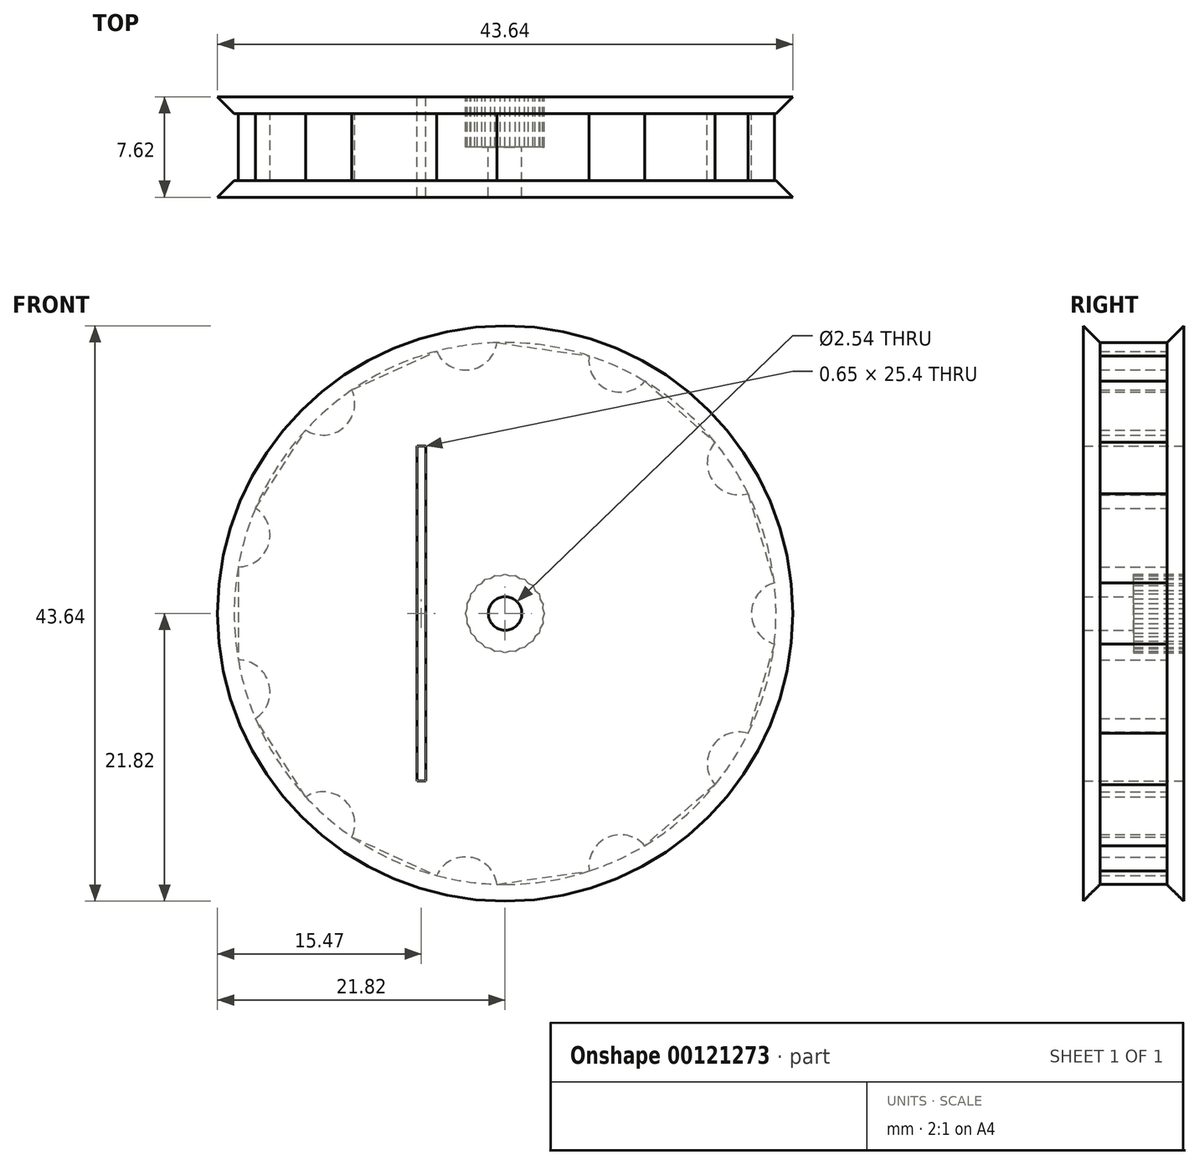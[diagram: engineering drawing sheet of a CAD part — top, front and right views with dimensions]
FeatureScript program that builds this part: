
annotation { "Feature Type Name" : "Feature", "Feature Type Description" : "" }
export const myFeature = defineFeature(function(context is Context, id is Id, definition is map)
    precondition{}
    {
        {
            var Q0;
            Q0=qCreatedBy(makeId("Front.planeOp"),FACE);
            var sketch = newSketch(context, id + "F0", { "sketchPlane" : qUnion([Q0])});
            skCircle(sketch, "E0", {"center": v(21.1, 0) * mm, "radius": 2.41 * mm});
            skCircle(sketch, "E1.1.0", {"center": v(17.75, 11.4) * mm, "radius": 2.41 * mm});
            skCircle(sketch, "E1.2.0", {"center": v(8.76, 19.2) * mm, "radius": 2.41 * mm});
            skCircle(sketch, "E1.3.0", {"center": v(-3, 20.88) * mm, "radius": 2.41 * mm});
            skCircle(sketch, "E1.4.0", {"center": v(-13.82, 15.94) * mm, "radius": 2.41 * mm});
            skCircle(sketch, "E1.5.0", {"center": v(-20.24, 5.94) * mm, "radius": 2.41 * mm});
            skPoint(sketch, "E1.center", {"position": v(0, 0) * mm});
            skCircle(sketch, "E2.1.6.0", {"center": v(-20.24, -5.94) * mm, "radius": 2.41 * mm});
            skLineSegment(sketch, "E3", {"start": v(-3, 20.88) * mm, "end": v(8.76, 19.2) * mm});
            skLineSegment(sketch, "E4", {"start": v(8.76, 19.2) * mm, "end": v(17.75, 11.4) * mm});
            skLineSegment(sketch, "E5", {"start": v(17.75, 11.4) * mm, "end": v(21.1, 0) * mm});
            skLineSegment(sketch, "E6", {"start": v(21.1, 0) * mm, "end": v(17.75, -11.4) * mm});
            skLineSegment(sketch, "E7", {"start": v(-20.24, 5.94) * mm, "end": v(-13.82, 15.94) * mm});
            skLineSegment(sketch, "E8", {"start": v(-13.82, 15.94) * mm, "end": v(-3, 20.88) * mm});
            skCircle(sketch, "E9.1.7.0", {"center": v(-13.82, -15.94) * mm, "radius": 2.41 * mm});
            skCircle(sketch, "E9.1.8.0", {"center": v(-3, -20.88) * mm, "radius": 2.41 * mm});
            skCircle(sketch, "E9.1.9.0", {"center": v(8.76, -19.2) * mm, "radius": 2.41 * mm});
            skLineSegment(sketch, "E10", {"start": v(-20.24, 5.94) * mm, "end": v(-20.24, -5.94) * mm});
            skLineSegment(sketch, "E11", {"start": v(-13.82, -15.94) * mm, "end": v(-20.24, -5.94) * mm});
            skLineSegment(sketch, "E12", {"start": v(-13.82, -15.94) * mm, "end": v(-3, -20.88) * mm});
            skCircle(sketch, "E13.1.10.0", {"center": v(17.75, -11.4) * mm, "radius": 2.41 * mm});
            skLineSegment(sketch, "E14", {"start": v(-3, -20.88) * mm, "end": v(8.76, -19.2) * mm});
            skLineSegment(sketch, "E15", {"start": v(17.75, -11.4) * mm, "end": v(8.76, -19.2) * mm});
            skCircle(sketch, "E16", {"center": v(0, 0) * mm, "radius": 1.27 * mm});
            skLineSegment(sketch, "E17", {"start": v(0, 0) * mm, "end": v(-6.35, 0) * mm, "construction": true});
            skLineSegment(sketch, "E18.bottom", {"start": v(-6.03, 12.7) * mm, "end": v(-6.67, 12.7) * mm});
            skLineSegment(sketch, "E18.top", {"start": v(-6.03, -12.7) * mm, "end": v(-6.67, -12.7) * mm});
            skLineSegment(sketch, "E18.left", {"start": v(-6.03, 12.7) * mm, "end": v(-6.03, -12.7) * mm});
            skLineSegment(sketch, "E18.right", {"start": v(-6.67, 12.7) * mm, "end": v(-6.67, -12.7) * mm});
            skPoint(sketch, "E18.middle", {"position": v(-6.35, 0) * mm});
            skSolve(sketch);
        }
        {
            var Q0;
            {var subQ22=sQuery(id+"F0.wireOp",EDGE,"E5");var subQ23=sQuery(id+"F0.wireOp",EDGE,"E0");var subQ24=makeQuery(id+"F0.imprint","INTERSECT",VERTEX,{"derivedFrom":[subQ23,subQ22]});Q0=makeQuery(id+"F0.imprint","IMPRINT",FACE,{"disambiguationData":[TD([[makeQuery(id+"F0.imprint","IMPRINT",EDGE,{"disambiguationData":[TD([[subQ24,-1.0]])],"derivedFrom":subQ23}),-1.0]])]});}
            extrude(context, id + "F1", {"entities" : qUnion([Q0]), "endBound" : BoundingType.SYMMETRIC, "depth" : 5.08 * mm});
        }
        {
            var Q0;
            Q0=makeQuery(id+"F1.opExtrude","CAP_FACE",FACE,{"disambiguationData":[OSD([sQuery(id+"F0.wireOp",EDGE,"E0"),sQuery(id+"F0.wireOp",EDGE,"E1.1.0"),sQuery(id+"F0.wireOp",EDGE,"E1.2.0"),sQuery(id+"F0.wireOp",EDGE,"E1.3.0"),sQuery(id+"F0.wireOp",EDGE,"E1.4.0"),sQuery(id+"F0.wireOp",EDGE,"E1.5.0"),sQuery(id+"F0.wireOp",EDGE,"E2.1.6.0"),sQuery(id+"F0.wireOp",EDGE,"E3"),sQuery(id+"F0.wireOp",EDGE,"E4"),sQuery(id+"F0.wireOp",EDGE,"E5"),sQuery(id+"F0.wireOp",EDGE,"E6"),sQuery(id+"F0.wireOp",EDGE,"k3TeTAbi-IA3Q-FxME-Idnx-3CxbzsMN8JZN"),sQuery(id+"F0.wireOp",EDGE,"E7"),sQuery(id+"F0.wireOp",EDGE,"E8")])],"isStart":false});
            var sketch = newSketch(context, id + "F2", { "sketchPlane" : qUnion([Q0])});
            skCircle(sketch, "E19", {"center": v(0, 0) * mm, "radius": 21.82 * mm});
            skCircle(sketch, "E20", {"center": v(0, 0) * mm, "radius": 1.27 * mm});
            skLineSegment(sketch, "E21", {"start": v(0, 0) * mm, "end": v(-6.35, 0) * mm, "construction": true});
            skLineSegment(sketch, "E22.bottom", {"start": v(-6.03, 12.7) * mm, "end": v(-6.67, 12.7) * mm});
            skLineSegment(sketch, "E22.top", {"start": v(-6.03, -12.7) * mm, "end": v(-6.67, -12.7) * mm});
            skLineSegment(sketch, "E22.left", {"start": v(-6.03, 12.7) * mm, "end": v(-6.03, -12.7) * mm});
            skLineSegment(sketch, "E22.right", {"start": v(-6.67, 12.7) * mm, "end": v(-6.67, -12.7) * mm});
            skPoint(sketch, "E22.middle", {"position": v(-6.35, 0) * mm});
            skSolve(sketch);
        }
        {
            var Q0;
            Q0 = qSketchRegion(id + "F2", true);
            extrude(context, id + "F3", {"entities" : qUnion([Q0]), "operationType" : NewBodyOperationType.ADD, "depth" : 1.27 * mm});
        }
        {
            var Q0;
            Q0=makeQuery(id+"F3.opExtrude","CAP_EDGE",EDGE,{"disambiguationData":[OSD([sQuery(id+"F2.wireOp",EDGE,"E19")])],"isStart":true});
            chamfer(context, id + "F4", {"entities" : qUnion([Q0]), "width" : 1.27 * mm, "tangentPropagation" : true});
        }
        {
            var Q0;
            Q0=makeQuery(id+"F1.opExtrude","SWEPT_BODY",BODY,{"disambiguationData":[OSD([sQuery(id+"F0.wireOp",EDGE,"E0"),sQuery(id+"F0.wireOp",EDGE,"E1.1.0"),sQuery(id+"F0.wireOp",EDGE,"E1.2.0"),sQuery(id+"F0.wireOp",EDGE,"E1.3.0"),sQuery(id+"F0.wireOp",EDGE,"E1.4.0"),sQuery(id+"F0.wireOp",EDGE,"E1.5.0"),sQuery(id+"F0.wireOp",EDGE,"E2.1.6.0"),sQuery(id+"F0.wireOp",EDGE,"E3"),sQuery(id+"F0.wireOp",EDGE,"E4"),sQuery(id+"F0.wireOp",EDGE,"E5"),sQuery(id+"F0.wireOp",EDGE,"E6"),sQuery(id+"F0.wireOp",EDGE,"k3TeTAbi-IA3Q-FxME-Idnx-3CxbzsMN8JZN"),sQuery(id+"F0.wireOp",EDGE,"E7"),sQuery(id+"F0.wireOp",EDGE,"E8")])]});
            var Q1;
            Q1=qCreatedBy(makeId("Front.planeOp"),FACE);
            mirror(context, id + "F5", {"operationType" : NewBodyOperationType.ADD, "entities" : qUnion([Q0]), "mirrorPlane" : qUnion([Q1])});
        }
        {
            var Q0;
            Q0=makeQuery(id+"F5.opPattern","COPY",FACE,{"derivedFrom":makeQuery(id+"F3.opExtrude","CAP_FACE",FACE,{"disambiguationData":[OSD([sQuery(id+"F2.wireOp",EDGE,"E19")])],"isStart":false}),"instanceName":"1"});
            var sketch = newSketch(context, id + "F6", { "sketchPlane" : qUnion([Q0])});
            skCircle(sketch, "E23.cCircle", {"center": v(0, 0) * mm, "radius": 2.86 * mm, "construction": true});
            skLineSegment(sketch, "E23.0", {"start": v(2.66, -1.1) * mm, "end": v(2.29, -1.75) * mm, "construction": true});
            skLineSegment(sketch, "E23.1", {"start": v(2.29, -1.75) * mm, "end": v(1.75, -2.29) * mm, "construction": true});
            skLineSegment(sketch, "E23.2", {"start": v(1.75, -2.29) * mm, "end": v(1.1, -2.66) * mm, "construction": true});
            skLineSegment(sketch, "E23.3", {"start": v(1.1, -2.66) * mm, "end": v(0.38, -2.86) * mm, "construction": true});
            skLineSegment(sketch, "E23.4", {"start": v(0.38, -2.86) * mm, "end": v(-0.38, -2.86) * mm, "construction": true});
            skLineSegment(sketch, "E23.5", {"start": v(-0.38, -2.86) * mm, "end": v(-1.1, -2.66) * mm, "construction": true});
            skLineSegment(sketch, "E23.6", {"start": v(-1.1, -2.66) * mm, "end": v(-1.75, -2.29) * mm, "construction": true});
            skLineSegment(sketch, "E23.7", {"start": v(-1.75, -2.29) * mm, "end": v(-2.29, -1.75) * mm, "construction": true});
            skLineSegment(sketch, "E23.8", {"start": v(-2.29, -1.75) * mm, "end": v(-2.66, -1.1) * mm, "construction": true});
            skLineSegment(sketch, "E23.9", {"start": v(-2.66, -1.1) * mm, "end": v(-2.86, -0.38) * mm, "construction": true});
            skLineSegment(sketch, "E23.10", {"start": v(-2.86, -0.38) * mm, "end": v(-2.86, 0.38) * mm, "construction": true});
            skLineSegment(sketch, "E23.11", {"start": v(-2.86, 0.38) * mm, "end": v(-2.66, 1.1) * mm, "construction": true});
            skLineSegment(sketch, "E23.12", {"start": v(-2.66, 1.1) * mm, "end": v(-2.29, 1.75) * mm, "construction": true});
            skLineSegment(sketch, "E23.13", {"start": v(-2.29, 1.75) * mm, "end": v(-1.75, 2.29) * mm, "construction": true});
            skLineSegment(sketch, "E23.14", {"start": v(-1.75, 2.29) * mm, "end": v(-1.1, 2.66) * mm, "construction": true});
            skLineSegment(sketch, "E23.15", {"start": v(-1.1, 2.66) * mm, "end": v(-0.38, 2.86) * mm, "construction": true});
            skLineSegment(sketch, "E23.16", {"start": v(-0.38, 2.86) * mm, "end": v(0.38, 2.86) * mm, "construction": true});
            skLineSegment(sketch, "E23.17", {"start": v(0.38, 2.86) * mm, "end": v(1.1, 2.66) * mm, "construction": true});
            skLineSegment(sketch, "E23.18", {"start": v(1.1, 2.66) * mm, "end": v(1.75, 2.29) * mm, "construction": true});
            skLineSegment(sketch, "E23.19", {"start": v(1.75, 2.29) * mm, "end": v(2.29, 1.75) * mm, "construction": true});
            skLineSegment(sketch, "E23.20", {"start": v(2.29, 1.75) * mm, "end": v(2.66, 1.1) * mm, "construction": true});
            skLineSegment(sketch, "E23.21", {"start": v(2.66, 1.1) * mm, "end": v(2.86, 0.38) * mm, "construction": true});
            skLineSegment(sketch, "E23.22", {"start": v(2.86, 0.38) * mm, "end": v(2.86, -0.38) * mm, "construction": true});
            skLineSegment(sketch, "E23.23", {"start": v(2.86, -0.38) * mm, "end": v(2.66, -1.1) * mm, "construction": true});
            skPoint(sketch, "E23.0.midPoint", {"position": v(2.47, -1.43) * mm});
            skCircle(sketch, "E24.cCircle", {"center": v(0, 0) * mm, "radius": 2.98 * mm, "construction": true});
            skLineSegment(sketch, "E24.0", {"start": v(2.88, 0.77) * mm, "end": v(2.98, 0) * mm});
            skLineSegment(sketch, "E24.1", {"start": v(2.98, 0) * mm, "end": v(2.88, -0.77) * mm});
            skLineSegment(sketch, "E24.2", {"start": v(2.88, -0.77) * mm, "end": v(2.58, -1.5) * mm});
            skLineSegment(sketch, "E24.3", {"start": v(2.58, -1.5) * mm, "end": v(2.11, -2.11) * mm});
            skLineSegment(sketch, "E24.4", {"start": v(2.11, -2.11) * mm, "end": v(1.5, -2.58) * mm});
            skLineSegment(sketch, "E24.5", {"start": v(1.5, -2.58) * mm, "end": v(0.77, -2.88) * mm});
            skLineSegment(sketch, "E24.6", {"start": v(0.77, -2.88) * mm, "end": v(0, -2.98) * mm});
            skLineSegment(sketch, "E24.7", {"start": v(0, -2.98) * mm, "end": v(-0.77, -2.88) * mm});
            skLineSegment(sketch, "E24.8", {"start": v(-0.77, -2.88) * mm, "end": v(-1.5, -2.58) * mm});
            skLineSegment(sketch, "E24.9", {"start": v(-1.5, -2.58) * mm, "end": v(-2.11, -2.11) * mm});
            skLineSegment(sketch, "E24.10", {"start": v(-2.11, -2.11) * mm, "end": v(-2.58, -1.5) * mm});
            skLineSegment(sketch, "E24.11", {"start": v(-2.58, -1.5) * mm, "end": v(-2.88, -0.77) * mm});
            skLineSegment(sketch, "E24.12", {"start": v(-2.88, -0.77) * mm, "end": v(-2.98, 0) * mm});
            skLineSegment(sketch, "E24.13", {"start": v(-2.98, 0) * mm, "end": v(-2.88, 0.77) * mm});
            skLineSegment(sketch, "E24.14", {"start": v(-2.88, 0.77) * mm, "end": v(-2.58, 1.5) * mm});
            skLineSegment(sketch, "E24.15", {"start": v(-2.58, 1.5) * mm, "end": v(-2.11, 2.11) * mm});
            skLineSegment(sketch, "E24.16", {"start": v(-2.11, 2.11) * mm, "end": v(-1.5, 2.58) * mm});
            skLineSegment(sketch, "E24.17", {"start": v(-1.5, 2.58) * mm, "end": v(-0.77, 2.88) * mm});
            skLineSegment(sketch, "E24.18", {"start": v(-0.77, 2.88) * mm, "end": v(0, 2.98) * mm});
            skLineSegment(sketch, "E24.19", {"start": v(0, 2.98) * mm, "end": v(0.77, 2.88) * mm});
            skLineSegment(sketch, "E24.20", {"start": v(0.77, 2.88) * mm, "end": v(1.5, 2.58) * mm});
            skLineSegment(sketch, "E24.21", {"start": v(1.5, 2.58) * mm, "end": v(2.11, 2.11) * mm});
            skLineSegment(sketch, "E24.22", {"start": v(2.11, 2.11) * mm, "end": v(2.58, 1.5) * mm});
            skLineSegment(sketch, "E24.23", {"start": v(2.58, 1.5) * mm, "end": v(2.88, 0.77) * mm});
            skLineSegment(sketch, "E25", {"start": v(-2.88, 0.77) * mm, "end": v(-2.66, 1.1) * mm});
            skLineSegment(sketch, "E26", {"start": v(-2.88, 0.77) * mm, "end": v(-2.86, 0.38) * mm});
            skLineSegment(sketch, "E27", {"start": v(0, 0) * mm, "end": v(-3.6, 0) * mm, "construction": true});
            skLineSegment(sketch, "E28", {"start": v(-2.86, 0.38) * mm, "end": v(-2.98, 0) * mm});
            skLineSegment(sketch, "E29", {"start": v(-2.98, 0) * mm, "end": v(-2.86, -0.38) * mm});
            skLineSegment(sketch, "E30.1.0", {"start": v(-2.86, -0.38) * mm, "end": v(-2.88, -0.77) * mm});
            skLineSegment(sketch, "E30.1.1", {"start": v(-2.88, -0.77) * mm, "end": v(-2.66, -1.1) * mm});
            skLineSegment(sketch, "E30.2.0", {"start": v(-2.66, -1.1) * mm, "end": v(-2.58, -1.5) * mm});
            skLineSegment(sketch, "E30.2.1", {"start": v(-2.58, -1.5) * mm, "end": v(-2.29, -1.75) * mm});
            skLineSegment(sketch, "E30.3.0", {"start": v(-2.29, -1.75) * mm, "end": v(-2.11, -2.11) * mm});
            skLineSegment(sketch, "E30.3.1", {"start": v(-2.11, -2.11) * mm, "end": v(-1.75, -2.29) * mm});
            skLineSegment(sketch, "E30.4.0", {"start": v(-1.75, -2.29) * mm, "end": v(-1.5, -2.58) * mm});
            skLineSegment(sketch, "E30.4.1", {"start": v(-1.5, -2.58) * mm, "end": v(-1.1, -2.66) * mm});
            skLineSegment(sketch, "E30.5.0", {"start": v(-1.1, -2.66) * mm, "end": v(-0.77, -2.88) * mm});
            skLineSegment(sketch, "E30.5.1", {"start": v(-0.77, -2.88) * mm, "end": v(-0.38, -2.86) * mm});
            skLineSegment(sketch, "E30.6.0", {"start": v(-0.38, -2.86) * mm, "end": v(0, -2.98) * mm});
            skLineSegment(sketch, "E30.6.1", {"start": v(0, -2.98) * mm, "end": v(0.38, -2.86) * mm});
            skLineSegment(sketch, "E30.7.0", {"start": v(0.38, -2.86) * mm, "end": v(0.77, -2.88) * mm});
            skLineSegment(sketch, "E30.7.1", {"start": v(0.77, -2.88) * mm, "end": v(1.1, -2.66) * mm});
            skLineSegment(sketch, "E30.8.0", {"start": v(1.1, -2.66) * mm, "end": v(1.5, -2.58) * mm});
            skLineSegment(sketch, "E30.8.1", {"start": v(1.5, -2.58) * mm, "end": v(1.75, -2.29) * mm});
            skLineSegment(sketch, "E30.9.0", {"start": v(1.75, -2.29) * mm, "end": v(2.11, -2.11) * mm});
            skLineSegment(sketch, "E30.9.1", {"start": v(2.11, -2.11) * mm, "end": v(2.29, -1.75) * mm});
            skLineSegment(sketch, "E30.10.0", {"start": v(2.29, -1.75) * mm, "end": v(2.58, -1.5) * mm});
            skLineSegment(sketch, "E30.10.1", {"start": v(2.58, -1.5) * mm, "end": v(2.66, -1.1) * mm});
            skLineSegment(sketch, "E30.11.0", {"start": v(2.66, -1.1) * mm, "end": v(2.88, -0.77) * mm});
            skLineSegment(sketch, "E30.11.1", {"start": v(2.88, -0.77) * mm, "end": v(2.86, -0.38) * mm});
            skLineSegment(sketch, "E30.12.0", {"start": v(2.86, -0.38) * mm, "end": v(2.98, 0) * mm});
            skLineSegment(sketch, "E30.12.1", {"start": v(2.98, 0) * mm, "end": v(2.86, 0.38) * mm});
            skLineSegment(sketch, "E30.13.0", {"start": v(2.86, 0.38) * mm, "end": v(2.88, 0.77) * mm});
            skLineSegment(sketch, "E30.13.1", {"start": v(2.88, 0.77) * mm, "end": v(2.66, 1.1) * mm});
            skLineSegment(sketch, "E30.14.0", {"start": v(2.66, 1.1) * mm, "end": v(2.58, 1.5) * mm});
            skLineSegment(sketch, "E30.14.1", {"start": v(2.58, 1.5) * mm, "end": v(2.29, 1.75) * mm});
            skLineSegment(sketch, "E30.15.0", {"start": v(2.29, 1.75) * mm, "end": v(2.11, 2.11) * mm});
            skLineSegment(sketch, "E30.15.1", {"start": v(2.11, 2.11) * mm, "end": v(1.75, 2.29) * mm});
            skLineSegment(sketch, "E30.16.0", {"start": v(1.75, 2.29) * mm, "end": v(1.5, 2.58) * mm});
            skLineSegment(sketch, "E30.16.1", {"start": v(1.5, 2.58) * mm, "end": v(1.1, 2.66) * mm});
            skLineSegment(sketch, "E30.17.0", {"start": v(1.1, 2.66) * mm, "end": v(0.77, 2.88) * mm});
            skLineSegment(sketch, "E30.17.1", {"start": v(0.77, 2.88) * mm, "end": v(0.38, 2.86) * mm});
            skLineSegment(sketch, "E30.18.0", {"start": v(0.38, 2.86) * mm, "end": v(0, 2.98) * mm});
            skLineSegment(sketch, "E30.18.1", {"start": v(0, 2.98) * mm, "end": v(-0.38, 2.86) * mm});
            skLineSegment(sketch, "E30.19.0", {"start": v(-0.38, 2.86) * mm, "end": v(-0.77, 2.88) * mm});
            skLineSegment(sketch, "E30.19.1", {"start": v(-0.77, 2.88) * mm, "end": v(-1.1, 2.66) * mm});
            skLineSegment(sketch, "E30.20.0", {"start": v(-1.1, 2.66) * mm, "end": v(-1.5, 2.58) * mm});
            skLineSegment(sketch, "E30.20.1", {"start": v(-1.5, 2.58) * mm, "end": v(-1.75, 2.29) * mm});
            skLineSegment(sketch, "E30.21.0", {"start": v(-1.75, 2.29) * mm, "end": v(-2.11, 2.11) * mm});
            skLineSegment(sketch, "E30.21.1", {"start": v(-2.11, 2.11) * mm, "end": v(-2.29, 1.75) * mm});
            skLineSegment(sketch, "E30.22.0", {"start": v(-2.29, 1.75) * mm, "end": v(-2.58, 1.5) * mm});
            skLineSegment(sketch, "E30.22.1", {"start": v(-2.58, 1.5) * mm, "end": v(-2.66, 1.1) * mm});
            skLineSegment(sketch, "E30.23.0", {"start": v(-2.66, 1.1) * mm, "end": v(-2.88, 0.77) * mm});
            skSolve(sketch);
        }
        {
            var Q0;
            Q0=makeQuery(id+"F6.imprint","IMPRINT",FACE,{"disambiguationData":[TD([[makeQuery(id+"F6.imprint","IMPRINT",EDGE,{"derivedFrom":sQuery(id+"F6.wireOp",EDGE,"E28")}),1.0]])]});
            extrude(context, id + "F7", {"entities" : qUnion([Q0]), "operationType" : NewBodyOperationType.REMOVE, "oppositeDirection" : true, "depth" : 3.8 * mm});
        }
    });
